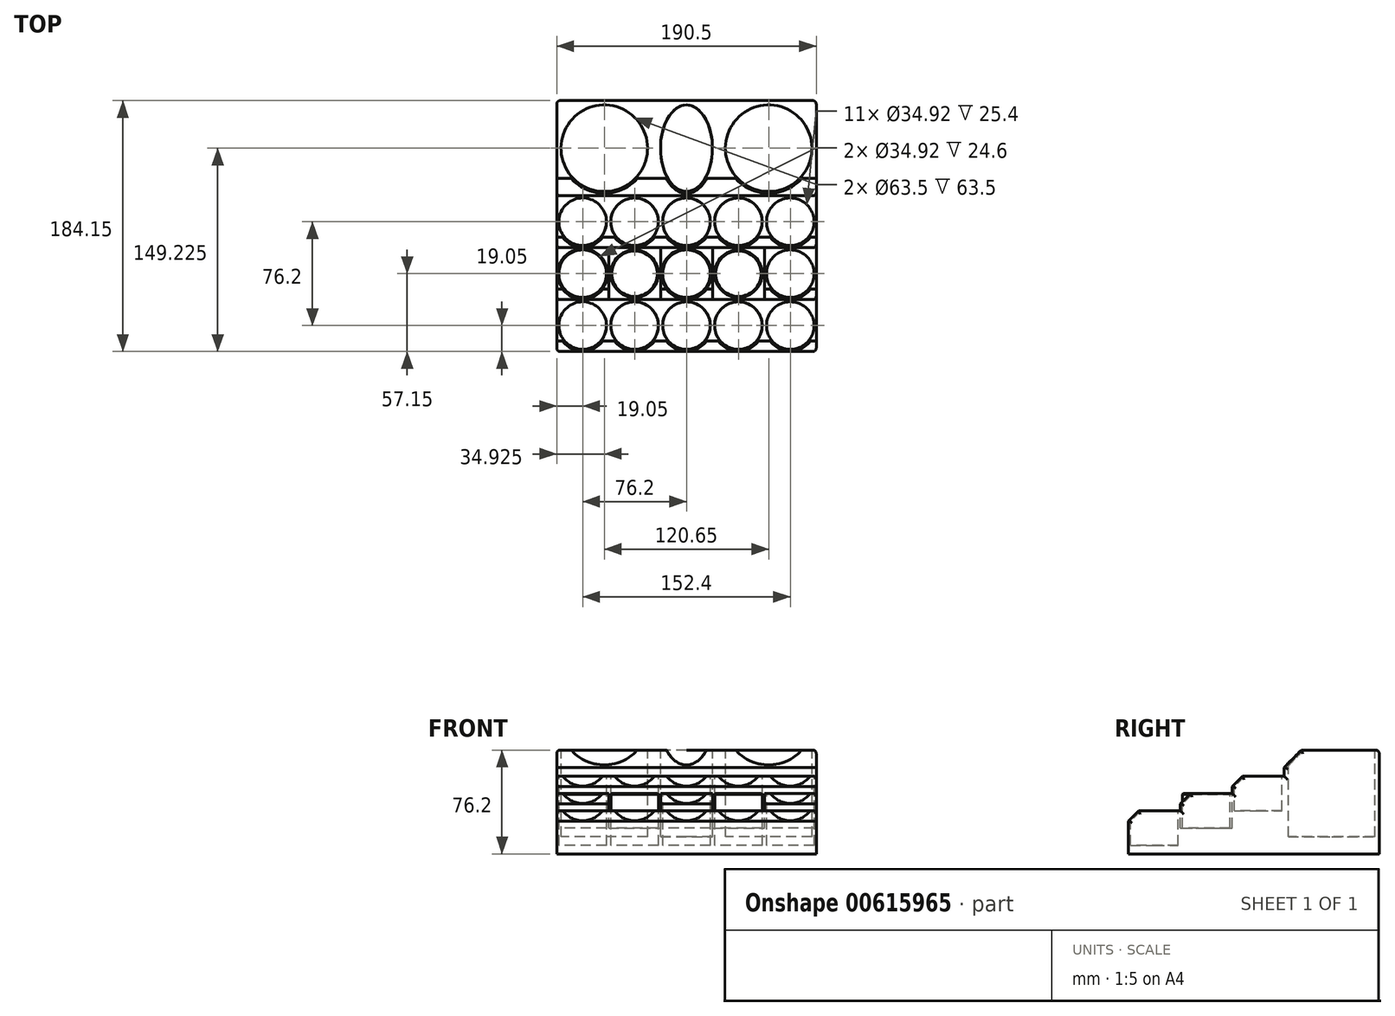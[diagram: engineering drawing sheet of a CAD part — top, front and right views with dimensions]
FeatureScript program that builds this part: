
annotation { "Feature Type Name" : "Feature", "Feature Type Description" : "" }
export const myFeature = defineFeature(function(context is Context, id is Id, definition is map)
    precondition{}
    {
        {
            var Q0;
            Q0=qCreatedBy(makeId("Right.planeOp"),FACE);
            var sketch = newSketch(context, id + "F0", { "sketchPlane" : qUnion([Q0])});
            skLineSegment(sketch, "E0", {"start": v(0, 0) * mm, "end": v(0, 31.75) * mm});
            skLineSegment(sketch, "E1", {"start": v(0, 31.75) * mm, "end": v(38.1, 31.75) * mm});
            skLineSegment(sketch, "E2", {"start": v(38.1, 31.75) * mm, "end": v(38.1, 44.45) * mm});
            skLineSegment(sketch, "E3", {"start": v(38.1, 44.45) * mm, "end": v(76.2, 44.45) * mm});
            skLineSegment(sketch, "E4", {"start": v(76.2, 44.45) * mm, "end": v(76.2, 57.15) * mm});
            skLineSegment(sketch, "E5", {"start": v(76.2, 57.15) * mm, "end": v(114.3, 57.15) * mm});
            skLineSegment(sketch, "E6", {"start": v(114.3, 57.15) * mm, "end": v(114.3, 76.2) * mm});
            skLineSegment(sketch, "E7", {"start": v(114.3, 76.2) * mm, "end": v(184.15, 76.2) * mm});
            skLineSegment(sketch, "E8", {"start": v(184.15, 76.2) * mm, "end": v(184.15, 0) * mm});
            skLineSegment(sketch, "E9", {"start": v(184.15, 0) * mm, "end": v(0, 0) * mm});
            skSolve(sketch);
        }
        {
            var Q0;
            Q0=qSketchRegion(id+"F0",true);
            extrude(context, id + "F1", {"entities" : qUnion([Q0]), "oppositeDirection" : true, "depth" : 190.5 * mm});
        }
        {
            var Q0;
            Q0=makeQuery(id+"F1.opExtrude","SWEPT_FACE",FACE,{"disambiguationData":[OSD([sQuery(id+"F0.wireOp",EDGE,"E1")])]});
            var sketch = newSketch(context, id + "F2", { "sketchPlane" : qUnion([Q0])});
            skLineSegment(sketch, "E10.bottom", {"start": v(-190.5, 0) * mm, "end": v(-152.4, 0) * mm, "construction": true});
            skLineSegment(sketch, "E10.top", {"start": v(-190.5, 38.1) * mm, "end": v(-152.4, 38.1) * mm, "construction": true});
            skLineSegment(sketch, "E10.left", {"start": v(-190.5, 0) * mm, "end": v(-190.5, 38.1) * mm, "construction": true});
            skLineSegment(sketch, "E10.right", {"start": v(-152.4, 0) * mm, "end": v(-152.4, 38.1) * mm, "construction": true});
            skLineSegment(sketch, "E11.bottom", {"start": v(-152.4, 0) * mm, "end": v(-114.3, 0) * mm, "construction": true});
            skLineSegment(sketch, "E11.top", {"start": v(-152.4, 38.1) * mm, "end": v(-114.3, 38.1) * mm, "construction": true});
            skLineSegment(sketch, "E11.right", {"start": v(-114.3, 0) * mm, "end": v(-114.3, 38.1) * mm, "construction": true});
            skLineSegment(sketch, "E12.bottom", {"start": v(-114.3, 0) * mm, "end": v(-76.2, 0) * mm, "construction": true});
            skLineSegment(sketch, "E12.top", {"start": v(-114.3, 38.1) * mm, "end": v(-76.2, 38.1) * mm, "construction": true});
            skLineSegment(sketch, "E12.right", {"start": v(-76.2, 0) * mm, "end": v(-76.2, 38.1) * mm, "construction": true});
            skLineSegment(sketch, "E13.bottom", {"start": v(-76.2, 0) * mm, "end": v(-38.1, 0) * mm, "construction": true});
            skLineSegment(sketch, "E13.top", {"start": v(-76.2, 38.1) * mm, "end": v(-38.1, 38.1) * mm, "construction": true});
            skLineSegment(sketch, "E13.right", {"start": v(-38.1, 0) * mm, "end": v(-38.1, 38.1) * mm, "construction": true});
            skLineSegment(sketch, "E14.bottom", {"start": v(-38.1, 0) * mm, "end": v(0, 0) * mm, "construction": true});
            skLineSegment(sketch, "E14.top", {"start": v(-38.1, 38.1) * mm, "end": v(0, 38.1) * mm, "construction": true});
            skLineSegment(sketch, "E14.right", {"start": v(0, 0) * mm, "end": v(0, 38.1) * mm, "construction": true});
            skLineSegment(sketch, "E15.bottom", {"start": v(-190.5, 0) * mm, "end": v(0, 0) * mm, "construction": true});
            skLineSegment(sketch, "E15.top", {"start": v(-190.5, 19.05) * mm, "end": v(0, 19.05) * mm, "construction": true});
            skLineSegment(sketch, "E15.left", {"start": v(-190.5, 0) * mm, "end": v(-190.5, 19.05) * mm, "construction": true});
            skLineSegment(sketch, "E15.right", {"start": v(0, 0) * mm, "end": v(0, 19.05) * mm, "construction": true});
            skLineSegment(sketch, "E16", {"start": v(-171.45, 0) * mm, "end": v(-171.45, 19.05) * mm, "construction": true});
            skLineSegment(sketch, "E17", {"start": v(-133.35, 0) * mm, "end": v(-133.35, 19.05) * mm, "construction": true});
            skLineSegment(sketch, "E18", {"start": v(-95.25, 0) * mm, "end": v(-95.25, 19.05) * mm, "construction": true});
            skLineSegment(sketch, "E19", {"start": v(-57.15, 0) * mm, "end": v(-57.15, 19.05) * mm, "construction": true});
            skLineSegment(sketch, "E20", {"start": v(-19.05, 0) * mm, "end": v(-19.05, 19.05) * mm, "construction": true});
            skCircle(sketch, "E21", {"center": v(-171.45, 19.05) * mm, "radius": 17.46 * mm});
            skCircle(sketch, "E22.MirrorC", {"center": v(-133.35, 19.05) * mm, "radius": 17.46 * mm});
            skCircle(sketch, "E23.MirrorC", {"center": v(-95.25, 19.05) * mm, "radius": 17.46 * mm});
            skCircle(sketch, "E24.MirrorC", {"center": v(-57.15, 19.05) * mm, "radius": 17.46 * mm});
            skCircle(sketch, "E25.MirrorC", {"center": v(-19.05, 19.05) * mm, "radius": 17.46 * mm});
            skSolve(sketch);
        }
        {
            var Q0;
            Q0=qSketchRegion(id+"F2",true);
            extrude(context, id + "F3", {"entities" : qUnion([Q0]), "operationType" : NewBodyOperationType.REMOVE, "oppositeDirection" : true, "depth" : 25.4 * mm});
        }
        {
            var Q0;
            Q0=makeQuery(id+"F1.opExtrude","SWEPT_FACE",FACE,{"disambiguationData":[OSD([sQuery(id+"F0.wireOp",EDGE,"E3")])]});
            var sketch = newSketch(context, id + "F4", { "sketchPlane" : qUnion([Q0])});
            skLineSegment(sketch, "E26.bottom", {"start": v(-190.5, 38.1) * mm, "end": v(-152.4, 38.1) * mm});
            skLineSegment(sketch, "E26.top", {"start": v(-190.5, 76.2) * mm, "end": v(-152.4, 76.2) * mm});
            skLineSegment(sketch, "E26.left", {"start": v(-190.5, 38.1) * mm, "end": v(-190.5, 76.2) * mm});
            skLineSegment(sketch, "E26.right", {"start": v(-152.4, 38.1) * mm, "end": v(-152.4, 76.2) * mm});
            skLineSegment(sketch, "E27.bottom", {"start": v(-152.4, 76.2) * mm, "end": v(-114.3, 76.2) * mm});
            skLineSegment(sketch, "E27.top", {"start": v(-152.4, 38.1) * mm, "end": v(-114.3, 38.1) * mm});
            skLineSegment(sketch, "E27.left", {"start": v(-152.4, 76.2) * mm, "end": v(-152.4, 38.1) * mm});
            skLineSegment(sketch, "E27.right", {"start": v(-114.3, 76.2) * mm, "end": v(-114.3, 38.1) * mm});
            skLineSegment(sketch, "E28.bottom", {"start": v(-114.3, 38.1) * mm, "end": v(-76.2, 38.1) * mm});
            skLineSegment(sketch, "E28.top", {"start": v(-114.3, 76.2) * mm, "end": v(-76.2, 76.2) * mm});
            skLineSegment(sketch, "E28.left", {"start": v(-114.3, 38.1) * mm, "end": v(-114.3, 76.2) * mm});
            skLineSegment(sketch, "E28.right", {"start": v(-76.2, 38.1) * mm, "end": v(-76.2, 76.2) * mm});
            skLineSegment(sketch, "E29.bottom", {"start": v(-76.2, 76.2) * mm, "end": v(-38.1, 76.2) * mm});
            skLineSegment(sketch, "E29.top", {"start": v(-76.2, 38.1) * mm, "end": v(-38.1, 38.1) * mm});
            skLineSegment(sketch, "E29.left", {"start": v(-76.2, 76.2) * mm, "end": v(-76.2, 38.1) * mm});
            skLineSegment(sketch, "E29.right", {"start": v(-38.1, 76.2) * mm, "end": v(-38.1, 38.1) * mm});
            skLineSegment(sketch, "E30.bottom", {"start": v(-38.1, 38.1) * mm, "end": v(0, 38.1) * mm});
            skLineSegment(sketch, "E30.top", {"start": v(-38.1, 76.2) * mm, "end": v(0, 76.2) * mm});
            skLineSegment(sketch, "E30.left", {"start": v(-38.1, 38.1) * mm, "end": v(-38.1, 76.2) * mm});
            skLineSegment(sketch, "E30.right", {"start": v(0, 38.1) * mm, "end": v(0, 76.2) * mm});
            skLineSegment(sketch, "E31", {"start": v(-190.5, 57.15) * mm, "end": v(0, 57.15) * mm, "construction": true});
            skLineSegment(sketch, "E32", {"start": v(-171.45, 76.2) * mm, "end": v(-171.45, 38.1) * mm, "construction": true});
            skLineSegment(sketch, "E33", {"start": v(-133.35, 76.2) * mm, "end": v(-133.35, 38.1) * mm, "construction": true});
            skLineSegment(sketch, "E34", {"start": v(-95.25, 76.2) * mm, "end": v(-95.25, 38.1) * mm, "construction": true});
            skLineSegment(sketch, "E35", {"start": v(-57.15, 76.2) * mm, "end": v(-57.15, 38.1) * mm, "construction": true});
            skLineSegment(sketch, "E36", {"start": v(-19.05, 76.2) * mm, "end": v(-19.05, 38.1) * mm, "construction": true});
            skCircle(sketch, "E37", {"center": v(-171.45, 57.15) * mm, "radius": 17.46 * mm});
            skCircle(sketch, "E38.MirrorC", {"center": v(-133.35, 57.15) * mm, "radius": 17.46 * mm});
            skCircle(sketch, "E39.MirrorC", {"center": v(-95.25, 57.15) * mm, "radius": 17.46 * mm});
            skCircle(sketch, "E40.MirrorC", {"center": v(-57.15, 57.15) * mm, "radius": 17.46 * mm});
            skCircle(sketch, "E41.MirrorC", {"center": v(-19.05, 57.15) * mm, "radius": 17.46 * mm});
            skSolve(sketch);
        }
        {
            var Q0;
            Q0=makeQuery(id+"F4.imprint","IMPRINT",FACE,{"disambiguationData":[TD([[makeQuery(id+"F4.imprint","IMPRINT",EDGE,{"derivedFrom":sQuery(id+"F4.wireOp",EDGE,"E39.MirrorC")}),1.0]])]});
            var Q1;
            Q1=makeQuery(id+"F4.imprint","IMPRINT",FACE,{"disambiguationData":[TD([[makeQuery(id+"F4.imprint","IMPRINT",EDGE,{"derivedFrom":sQuery(id+"F4.wireOp",EDGE,"E38.MirrorC")}),-1.0]])]});
            var Q2;
            Q2=makeQuery(id+"F4.imprint","IMPRINT",FACE,{"disambiguationData":[TD([[makeQuery(id+"F4.imprint","IMPRINT",EDGE,{"derivedFrom":sQuery(id+"F4.wireOp",EDGE,"E37")}),1.0]])]});
            var Q3;
            Q3=makeQuery(id+"F4.imprint","IMPRINT",FACE,{"disambiguationData":[TD([[makeQuery(id+"F4.imprint","IMPRINT",EDGE,{"derivedFrom":sQuery(id+"F4.wireOp",EDGE,"E40.MirrorC")}),-1.0]])]});
            var Q4;
            Q4=makeQuery(id+"F4.imprint","IMPRINT",FACE,{"disambiguationData":[TD([[makeQuery(id+"F4.imprint","IMPRINT",EDGE,{"derivedFrom":sQuery(id+"F4.wireOp",EDGE,"E41.MirrorC")}),1.0]])]});
            extrude(context, id + "F5", {"entities" : qUnion([Q0, Q1, Q2, Q3, Q4]), "operationType" : NewBodyOperationType.REMOVE, "oppositeDirection" : true, "depth" : 25.4 * mm});
        }
        {
            var Q0;
            Q0=makeQuery(id+"F1.opExtrude","SWEPT_FACE",FACE,{"disambiguationData":[OSD([sQuery(id+"F0.wireOp",EDGE,"E5")])]});
            var sketch = newSketch(context, id + "F6", { "sketchPlane" : qUnion([Q0])});
            skLineSegment(sketch, "E42.bottom", {"start": v(-190.5, 114.3) * mm, "end": v(-152.4, 114.3) * mm, "construction": true});
            skLineSegment(sketch, "E42.top", {"start": v(-190.5, 76.2) * mm, "end": v(-152.4, 76.2) * mm, "construction": true});
            skLineSegment(sketch, "E42.left", {"start": v(-190.5, 114.3) * mm, "end": v(-190.5, 76.2) * mm, "construction": true});
            skLineSegment(sketch, "E42.right", {"start": v(-152.4, 114.3) * mm, "end": v(-152.4, 76.2) * mm, "construction": true});
            skLineSegment(sketch, "E43.bottom", {"start": v(-152.4, 76.2) * mm, "end": v(-114.3, 76.2) * mm, "construction": true});
            skLineSegment(sketch, "E43.top", {"start": v(-152.4, 114.3) * mm, "end": v(-114.3, 114.3) * mm, "construction": true});
            skLineSegment(sketch, "E43.left", {"start": v(-152.4, 76.2) * mm, "end": v(-152.4, 114.3) * mm, "construction": true});
            skLineSegment(sketch, "E43.right", {"start": v(-114.3, 76.2) * mm, "end": v(-114.3, 114.3) * mm, "construction": true});
            skLineSegment(sketch, "E44.bottom", {"start": v(-114.3, 114.3) * mm, "end": v(-76.2, 114.3) * mm, "construction": true});
            skLineSegment(sketch, "E44.top", {"start": v(-114.3, 76.2) * mm, "end": v(-76.2, 76.2) * mm, "construction": true});
            skLineSegment(sketch, "E44.left", {"start": v(-114.3, 114.3) * mm, "end": v(-114.3, 76.2) * mm, "construction": true});
            skLineSegment(sketch, "E44.right", {"start": v(-76.2, 114.3) * mm, "end": v(-76.2, 76.2) * mm, "construction": true});
            skLineSegment(sketch, "E45.bottom", {"start": v(-76.2, 76.2) * mm, "end": v(-38.1, 76.2) * mm, "construction": true});
            skLineSegment(sketch, "E45.top", {"start": v(-76.2, 114.3) * mm, "end": v(-38.1, 114.3) * mm, "construction": true});
            skLineSegment(sketch, "E45.left", {"start": v(-76.2, 76.2) * mm, "end": v(-76.2, 114.3) * mm, "construction": true});
            skLineSegment(sketch, "E45.right", {"start": v(-38.1, 76.2) * mm, "end": v(-38.1, 114.3) * mm, "construction": true});
            skLineSegment(sketch, "E46.bottom", {"start": v(-38.1, 114.3) * mm, "end": v(0, 114.3) * mm, "construction": true});
            skLineSegment(sketch, "E46.top", {"start": v(-38.1, 76.2) * mm, "end": v(0, 76.2) * mm, "construction": true});
            skLineSegment(sketch, "E46.left", {"start": v(-38.1, 114.3) * mm, "end": v(-38.1, 76.2) * mm, "construction": true});
            skLineSegment(sketch, "E46.right", {"start": v(0, 114.3) * mm, "end": v(0, 76.2) * mm, "construction": true});
            skLineSegment(sketch, "E47", {"start": v(-190.5, 95.25) * mm, "end": v(0, 95.25) * mm, "construction": true});
            skLineSegment(sketch, "E48", {"start": v(-171.45, 76.2) * mm, "end": v(-171.45, 114.3) * mm, "construction": true});
            skLineSegment(sketch, "E49", {"start": v(-133.35, 114.3) * mm, "end": v(-133.35, 76.2) * mm, "construction": true});
            skLineSegment(sketch, "E50", {"start": v(-95.25, 114.3) * mm, "end": v(-95.25, 76.2) * mm, "construction": true});
            skLineSegment(sketch, "E51", {"start": v(-57.15, 114.3) * mm, "end": v(-57.15, 76.2) * mm, "construction": true});
            skLineSegment(sketch, "E52", {"start": v(-19.05, 114.3) * mm, "end": v(-19.05, 76.2) * mm, "construction": true});
            skCircle(sketch, "E53", {"center": v(-171.45, 95.25) * mm, "radius": 17.46 * mm});
            skCircle(sketch, "E54.MirrorC", {"center": v(-133.35, 95.25) * mm, "radius": 17.46 * mm});
            skCircle(sketch, "E55.MirrorC", {"center": v(-95.25, 95.25) * mm, "radius": 17.46 * mm});
            skCircle(sketch, "E56.MirrorC", {"center": v(-57.15, 95.25) * mm, "radius": 17.46 * mm});
            skCircle(sketch, "E57.MirrorC", {"center": v(-19.05, 95.25) * mm, "radius": 17.46 * mm});
            skSolve(sketch);
        }
        {
            var Q0;
            Q0=qSketchRegion(id+"F6",true);
            extrude(context, id + "F7", {"entities" : qUnion([Q0]), "operationType" : NewBodyOperationType.REMOVE, "oppositeDirection" : true, "depth" : 25.4 * mm});
        }
        {
            var Q0;
            Q0=makeQuery(id+"F1.opExtrude","SWEPT_FACE",FACE,{"disambiguationData":[OSD([sQuery(id+"F0.wireOp",EDGE,"E7")])]});
            var sketch = newSketch(context, id + "F8", { "sketchPlane" : qUnion([Q0])});
            skLineSegment(sketch, "E58.bottom", {"start": v(-190.5, 114.3) * mm, "end": v(-120.65, 114.3) * mm, "construction": true});
            skLineSegment(sketch, "E58.top", {"start": v(-190.5, 184.15) * mm, "end": v(-120.65, 184.15) * mm, "construction": true});
            skLineSegment(sketch, "E58.left", {"start": v(-190.5, 114.3) * mm, "end": v(-190.5, 184.15) * mm, "construction": true});
            skLineSegment(sketch, "E58.right", {"start": v(-120.65, 114.3) * mm, "end": v(-120.65, 184.15) * mm, "construction": true});
            skLineSegment(sketch, "E59.bottom", {"start": v(0, 114.3) * mm, "end": v(-69.85, 114.3) * mm, "construction": true});
            skLineSegment(sketch, "E59.top", {"start": v(0, 184.15) * mm, "end": v(-69.85, 184.15) * mm, "construction": true});
            skLineSegment(sketch, "E59.left", {"start": v(0, 114.3) * mm, "end": v(0, 184.15) * mm, "construction": true});
            skLineSegment(sketch, "E59.right", {"start": v(-69.85, 114.3) * mm, "end": v(-69.85, 184.15) * mm, "construction": true});
            skLineSegment(sketch, "E60", {"start": v(-155.58, 114.3) * mm, "end": v(-155.58, 184.15) * mm, "construction": true});
            skLineSegment(sketch, "E61", {"start": v(-34.93, 184.15) * mm, "end": v(-34.93, 114.3) * mm, "construction": true});
            skLineSegment(sketch, "E62", {"start": v(-190.5, 149.23) * mm, "end": v(0, 149.23) * mm, "construction": true});
            skLineSegment(sketch, "E63", {"start": v(-95.25, 184.15) * mm, "end": v(-95.25, 114.3) * mm, "construction": true});
            skCircle(sketch, "E64", {"center": v(-155.58, 149.23) * mm, "radius": 31.75 * mm});
            skCircle(sketch, "E65.MirrorC", {"center": v(-34.93, 149.23) * mm, "radius": 31.75 * mm});
            skEllipse(sketch, "E66", {"center": v(-95.25, 149.23) * mm, "majorRadius": 31.75 * mm, "minorRadius": 19.05 * mm, "majorAxis": v(0, 1)});
            skSolve(sketch);
        }
        {
            var Q0;
            Q0=qSketchRegion(id+"F8",true);
            extrude(context, id + "F9", {"entities" : qUnion([Q0]), "operationType" : NewBodyOperationType.REMOVE, "oppositeDirection" : true, "depth" : 63.5 * mm});
        }
        {
            var Q0;
            Q0=makeQuery(id+"F1.opExtrude","SWEPT_EDGE",EDGE,{"disambiguationData":[OSD([sQuery(id+"F0.wireOp",EDGE,"E4"),sQuery(id+"F0.wireOp",EDGE,"E5")])]});
            var Q1;
            Q1=makeQuery(id+"F1.opExtrude","SWEPT_EDGE",EDGE,{"disambiguationData":[OSD([sQuery(id+"F0.wireOp",EDGE,"E2"),sQuery(id+"F0.wireOp",EDGE,"E3")])]});
            var Q2;
            Q2=makeQuery(id+"F1.opExtrude","SWEPT_EDGE",EDGE,{"disambiguationData":[OSD([sQuery(id+"F0.wireOp",EDGE,"E0"),sQuery(id+"F0.wireOp",EDGE,"E1")])]});
            chamfer(context, id + "F10", {"entities" : qUnion([Q0, Q1, Q2]), "width" : 7.62 * mm});
        }
        {
            var Q0;
            Q0=makeQuery(id+"F1.opExtrude","SWEPT_EDGE",EDGE,{"disambiguationData":[OSD([sQuery(id+"F0.wireOp",EDGE,"E6"),sQuery(id+"F0.wireOp",EDGE,"E7")])]});
            chamfer(context, id + "F11", {"entities" : qUnion([Q0]), "width" : 12.7 * mm, "tangentPropagation" : true});
        }
        {
            var Q0;
            Q0=makeQuery(id+"F3.boolean.opBoolean","COPY",EDGE,{"derivedFrom":makeQuery(id+"F3.opExtrude","CAP_EDGE",EDGE,{"disambiguationData":[OSD([sQuery(id+"F2.wireOp",EDGE,"E21")])],"isStart":true})});
            var Q1;
            Q1=makeQuery(id+"F3.boolean.opBoolean","COPY",EDGE,{"derivedFrom":makeQuery(id+"F3.opExtrude","CAP_EDGE",EDGE,{"disambiguationData":[OSD([sQuery(id+"F2.wireOp",EDGE,"E22.MirrorC")])],"isStart":true})});
            var Q2;
            Q2=makeQuery(id+"F3.boolean.opBoolean","COPY",EDGE,{"derivedFrom":makeQuery(id+"F3.opExtrude","CAP_EDGE",EDGE,{"disambiguationData":[OSD([sQuery(id+"F2.wireOp",EDGE,"E23.MirrorC")])],"isStart":true})});
            var Q3;
            Q3=makeQuery(id+"F3.boolean.opBoolean","COPY",EDGE,{"derivedFrom":makeQuery(id+"F3.opExtrude","CAP_EDGE",EDGE,{"disambiguationData":[OSD([sQuery(id+"F2.wireOp",EDGE,"E24.MirrorC")])],"isStart":true})});
            var Q4;
            Q4=makeQuery(id+"F3.boolean.opBoolean","COPY",EDGE,{"derivedFrom":makeQuery(id+"F3.opExtrude","CAP_EDGE",EDGE,{"disambiguationData":[OSD([sQuery(id+"F2.wireOp",EDGE,"E25.MirrorC")])],"isStart":true})});
            var Q5;
            Q5=makeQuery(id+"F5.boolean.opBoolean","COPY",EDGE,{"derivedFrom":makeQuery(id+"F5.opExtrude","CAP_EDGE",EDGE,{"disambiguationData":[OSD([sQuery(id+"F4.wireOp",EDGE,"E41.MirrorC")])],"isStart":true})});
            var Q6;
            Q6=makeQuery(id+"F5.boolean.opBoolean","COPY",EDGE,{"derivedFrom":makeQuery(id+"F5.opExtrude","CAP_EDGE",EDGE,{"disambiguationData":[OSD([sQuery(id+"F4.wireOp",EDGE,"E40.MirrorC")])],"isStart":true})});
            var Q7;
            Q7=makeQuery(id+"F5.boolean.opBoolean","COPY",EDGE,{"derivedFrom":makeQuery(id+"F5.opExtrude","CAP_EDGE",EDGE,{"disambiguationData":[OSD([sQuery(id+"F4.wireOp",EDGE,"E39.MirrorC")])],"isStart":true})});
            var Q8;
            Q8=makeQuery(id+"F5.boolean.opBoolean","COPY",EDGE,{"derivedFrom":makeQuery(id+"F5.opExtrude","CAP_EDGE",EDGE,{"disambiguationData":[OSD([sQuery(id+"F4.wireOp",EDGE,"E38.MirrorC")])],"isStart":true})});
            var Q9;
            Q9=makeQuery(id+"F5.boolean.opBoolean","COPY",EDGE,{"derivedFrom":makeQuery(id+"F5.opExtrude","CAP_EDGE",EDGE,{"disambiguationData":[OSD([sQuery(id+"F4.wireOp",EDGE,"E37")])],"isStart":true})});
            var Q10;
            Q10=makeQuery(id+"F7.boolean.opBoolean","COPY",EDGE,{"derivedFrom":makeQuery(id+"F7.opExtrude","CAP_EDGE",EDGE,{"disambiguationData":[OSD([sQuery(id+"F6.wireOp",EDGE,"E53")])],"isStart":true})});
            var Q11;
            Q11=makeQuery(id+"F7.boolean.opBoolean","COPY",EDGE,{"derivedFrom":makeQuery(id+"F7.opExtrude","CAP_EDGE",EDGE,{"disambiguationData":[OSD([sQuery(id+"F6.wireOp",EDGE,"E54.MirrorC")])],"isStart":true})});
            var Q12;
            Q12=makeQuery(id+"F7.boolean.opBoolean","COPY",EDGE,{"derivedFrom":makeQuery(id+"F7.opExtrude","CAP_EDGE",EDGE,{"disambiguationData":[OSD([sQuery(id+"F6.wireOp",EDGE,"E55.MirrorC")])],"isStart":true})});
            var Q13;
            Q13=makeQuery(id+"F7.boolean.opBoolean","COPY",EDGE,{"derivedFrom":makeQuery(id+"F7.opExtrude","CAP_EDGE",EDGE,{"disambiguationData":[OSD([sQuery(id+"F6.wireOp",EDGE,"E56.MirrorC")])],"isStart":true})});
            var Q14;
            Q14=makeQuery(id+"F7.boolean.opBoolean","COPY",EDGE,{"derivedFrom":makeQuery(id+"F7.opExtrude","CAP_EDGE",EDGE,{"disambiguationData":[OSD([sQuery(id+"F6.wireOp",EDGE,"E57.MirrorC")])],"isStart":true})});
            var Q15;
            Q15=makeQuery(id+"F9.boolean.opBoolean","COPY",EDGE,{"derivedFrom":makeQuery(id+"F9.opExtrude","CAP_EDGE",EDGE,{"disambiguationData":[OSD([sQuery(id+"F8.wireOp",EDGE,"E65.MirrorC")])],"isStart":true})});
            var Q16;
            Q16=makeQuery(id+"F9.boolean.opBoolean","COPY",EDGE,{"derivedFrom":makeQuery(id+"F9.opExtrude","CAP_EDGE",EDGE,{"disambiguationData":[OSD([sQuery(id+"F8.wireOp",EDGE,"E66")])],"isStart":true})});
            var Q17;
            Q17=makeQuery(id+"F9.boolean.opBoolean","COPY",EDGE,{"derivedFrom":makeQuery(id+"F9.opExtrude","CAP_EDGE",EDGE,{"disambiguationData":[OSD([sQuery(id+"F8.wireOp",EDGE,"E64")])],"isStart":true})});
            var Q18;
            Q18=makeQuery(id+"F10.opChamfer","BLEND_EDGE",EDGE,{"blendedFrom":[makeQuery(id+"F1.opExtrude","SWEPT_EDGE",EDGE,{"disambiguationData":[OSD([sQuery(id+"F0.wireOp",EDGE,"E0"),sQuery(id+"F0.wireOp",EDGE,"E1")])]}),makeQuery(id+"F3.boolean.opBoolean","COPY",FACE,{"derivedFrom":makeQuery(id+"F3.opExtrude","SWEPT_FACE",FACE,{"disambiguationData":[OSD([sQuery(id+"F2.wireOp",EDGE,"E21")])]})})],"blendedInto":[makeQuery(id+"F3.boolean.opBoolean","COPY",FACE,{"derivedFrom":makeQuery(id+"F3.opExtrude","SWEPT_FACE",FACE,{"disambiguationData":[OSD([sQuery(id+"F2.wireOp",EDGE,"E21")])]})})]});
            var Q19;
            Q19=makeQuery(id+"F10.opChamfer","BLEND_EDGE",EDGE,{"blendedFrom":[makeQuery(id+"F1.opExtrude","SWEPT_EDGE",EDGE,{"disambiguationData":[OSD([sQuery(id+"F0.wireOp",EDGE,"E0"),sQuery(id+"F0.wireOp",EDGE,"E1")])]}),makeQuery(id+"F3.boolean.opBoolean","COPY",FACE,{"derivedFrom":makeQuery(id+"F3.opExtrude","SWEPT_FACE",FACE,{"disambiguationData":[OSD([sQuery(id+"F2.wireOp",EDGE,"E22.MirrorC")])]})})],"blendedInto":[makeQuery(id+"F3.boolean.opBoolean","COPY",FACE,{"derivedFrom":makeQuery(id+"F3.opExtrude","SWEPT_FACE",FACE,{"disambiguationData":[OSD([sQuery(id+"F2.wireOp",EDGE,"E22.MirrorC")])]})})]});
            var Q20;
            Q20=makeQuery(id+"F10.opChamfer","BLEND_EDGE",EDGE,{"blendedFrom":[makeQuery(id+"F1.opExtrude","SWEPT_EDGE",EDGE,{"disambiguationData":[OSD([sQuery(id+"F0.wireOp",EDGE,"E0"),sQuery(id+"F0.wireOp",EDGE,"E1")])]}),makeQuery(id+"F3.boolean.opBoolean","COPY",FACE,{"derivedFrom":makeQuery(id+"F3.opExtrude","SWEPT_FACE",FACE,{"disambiguationData":[OSD([sQuery(id+"F2.wireOp",EDGE,"E23.MirrorC")])]})})],"blendedInto":[makeQuery(id+"F3.boolean.opBoolean","COPY",FACE,{"derivedFrom":makeQuery(id+"F3.opExtrude","SWEPT_FACE",FACE,{"disambiguationData":[OSD([sQuery(id+"F2.wireOp",EDGE,"E23.MirrorC")])]})})]});
            var Q21;
            Q21=makeQuery(id+"F10.opChamfer","BLEND_EDGE",EDGE,{"blendedFrom":[makeQuery(id+"F1.opExtrude","SWEPT_EDGE",EDGE,{"disambiguationData":[OSD([sQuery(id+"F0.wireOp",EDGE,"E0"),sQuery(id+"F0.wireOp",EDGE,"E1")])]}),makeQuery(id+"F3.boolean.opBoolean","COPY",FACE,{"derivedFrom":makeQuery(id+"F3.opExtrude","SWEPT_FACE",FACE,{"disambiguationData":[OSD([sQuery(id+"F2.wireOp",EDGE,"E24.MirrorC")])]})})],"blendedInto":[makeQuery(id+"F3.boolean.opBoolean","COPY",FACE,{"derivedFrom":makeQuery(id+"F3.opExtrude","SWEPT_FACE",FACE,{"disambiguationData":[OSD([sQuery(id+"F2.wireOp",EDGE,"E24.MirrorC")])]})})]});
            var Q22;
            Q22=makeQuery(id+"F10.opChamfer","BLEND_EDGE",EDGE,{"blendedFrom":[makeQuery(id+"F1.opExtrude","SWEPT_EDGE",EDGE,{"disambiguationData":[OSD([sQuery(id+"F0.wireOp",EDGE,"E0"),sQuery(id+"F0.wireOp",EDGE,"E1")])]}),makeQuery(id+"F3.boolean.opBoolean","COPY",FACE,{"derivedFrom":makeQuery(id+"F3.opExtrude","SWEPT_FACE",FACE,{"disambiguationData":[OSD([sQuery(id+"F2.wireOp",EDGE,"E25.MirrorC")])]})})],"blendedInto":[makeQuery(id+"F3.boolean.opBoolean","COPY",FACE,{"derivedFrom":makeQuery(id+"F3.opExtrude","SWEPT_FACE",FACE,{"disambiguationData":[OSD([sQuery(id+"F2.wireOp",EDGE,"E25.MirrorC")])]})})]});
            var Q23;
            Q23=makeQuery(id+"F10.opChamfer","BLEND_EDGE",EDGE,{"blendedFrom":[makeQuery(id+"F1.opExtrude","SWEPT_EDGE",EDGE,{"disambiguationData":[OSD([sQuery(id+"F0.wireOp",EDGE,"E2"),sQuery(id+"F0.wireOp",EDGE,"E3")])]}),makeQuery(id+"F5.boolean.opBoolean","COPY",FACE,{"derivedFrom":makeQuery(id+"F5.opExtrude","SWEPT_FACE",FACE,{"disambiguationData":[OSD([sQuery(id+"F4.wireOp",EDGE,"E41.MirrorC")])]})})],"blendedInto":[makeQuery(id+"F5.boolean.opBoolean","COPY",FACE,{"derivedFrom":makeQuery(id+"F5.opExtrude","SWEPT_FACE",FACE,{"disambiguationData":[OSD([sQuery(id+"F4.wireOp",EDGE,"E41.MirrorC")])]})})]});
            var Q24;
            Q24=makeQuery(id+"F10.opChamfer","BLEND_EDGE",EDGE,{"blendedFrom":[makeQuery(id+"F1.opExtrude","SWEPT_EDGE",EDGE,{"disambiguationData":[OSD([sQuery(id+"F0.wireOp",EDGE,"E2"),sQuery(id+"F0.wireOp",EDGE,"E3")])]}),makeQuery(id+"F5.boolean.opBoolean","COPY",FACE,{"derivedFrom":makeQuery(id+"F5.opExtrude","SWEPT_FACE",FACE,{"disambiguationData":[OSD([sQuery(id+"F4.wireOp",EDGE,"E40.MirrorC")])]})})],"blendedInto":[makeQuery(id+"F5.boolean.opBoolean","COPY",FACE,{"derivedFrom":makeQuery(id+"F5.opExtrude","SWEPT_FACE",FACE,{"disambiguationData":[OSD([sQuery(id+"F4.wireOp",EDGE,"E40.MirrorC")])]})})]});
            var Q25;
            Q25=makeQuery(id+"F10.opChamfer","BLEND_EDGE",EDGE,{"blendedFrom":[makeQuery(id+"F1.opExtrude","SWEPT_EDGE",EDGE,{"disambiguationData":[OSD([sQuery(id+"F0.wireOp",EDGE,"E2"),sQuery(id+"F0.wireOp",EDGE,"E3")])]}),makeQuery(id+"F5.boolean.opBoolean","COPY",FACE,{"derivedFrom":makeQuery(id+"F5.opExtrude","SWEPT_FACE",FACE,{"disambiguationData":[OSD([sQuery(id+"F4.wireOp",EDGE,"E39.MirrorC")])]})})],"blendedInto":[makeQuery(id+"F5.boolean.opBoolean","COPY",FACE,{"derivedFrom":makeQuery(id+"F5.opExtrude","SWEPT_FACE",FACE,{"disambiguationData":[OSD([sQuery(id+"F4.wireOp",EDGE,"E39.MirrorC")])]})})]});
            var Q26;
            Q26=makeQuery(id+"F10.opChamfer","BLEND_EDGE",EDGE,{"blendedFrom":[makeQuery(id+"F1.opExtrude","SWEPT_EDGE",EDGE,{"disambiguationData":[OSD([sQuery(id+"F0.wireOp",EDGE,"E2"),sQuery(id+"F0.wireOp",EDGE,"E3")])]}),makeQuery(id+"F5.boolean.opBoolean","COPY",FACE,{"derivedFrom":makeQuery(id+"F5.opExtrude","SWEPT_FACE",FACE,{"disambiguationData":[OSD([sQuery(id+"F4.wireOp",EDGE,"E38.MirrorC")])]})})],"blendedInto":[makeQuery(id+"F5.boolean.opBoolean","COPY",FACE,{"derivedFrom":makeQuery(id+"F5.opExtrude","SWEPT_FACE",FACE,{"disambiguationData":[OSD([sQuery(id+"F4.wireOp",EDGE,"E38.MirrorC")])]})})]});
            var Q27;
            Q27=makeQuery(id+"F10.opChamfer","BLEND_EDGE",EDGE,{"blendedFrom":[makeQuery(id+"F1.opExtrude","SWEPT_EDGE",EDGE,{"disambiguationData":[OSD([sQuery(id+"F0.wireOp",EDGE,"E2"),sQuery(id+"F0.wireOp",EDGE,"E3")])]}),makeQuery(id+"F5.boolean.opBoolean","COPY",FACE,{"derivedFrom":makeQuery(id+"F5.opExtrude","SWEPT_FACE",FACE,{"disambiguationData":[OSD([sQuery(id+"F4.wireOp",EDGE,"E37")])]})})],"blendedInto":[makeQuery(id+"F5.boolean.opBoolean","COPY",FACE,{"derivedFrom":makeQuery(id+"F5.opExtrude","SWEPT_FACE",FACE,{"disambiguationData":[OSD([sQuery(id+"F4.wireOp",EDGE,"E37")])]})})]});
            var Q28;
            Q28=makeQuery(id+"F10.opChamfer","BLEND_EDGE",EDGE,{"blendedFrom":[makeQuery(id+"F1.opExtrude","SWEPT_EDGE",EDGE,{"disambiguationData":[OSD([sQuery(id+"F0.wireOp",EDGE,"E4"),sQuery(id+"F0.wireOp",EDGE,"E5")])]}),makeQuery(id+"F7.boolean.opBoolean","COPY",FACE,{"derivedFrom":makeQuery(id+"F7.opExtrude","SWEPT_FACE",FACE,{"disambiguationData":[OSD([sQuery(id+"F6.wireOp",EDGE,"E53")])]})})],"blendedInto":[makeQuery(id+"F7.boolean.opBoolean","COPY",FACE,{"derivedFrom":makeQuery(id+"F7.opExtrude","SWEPT_FACE",FACE,{"disambiguationData":[OSD([sQuery(id+"F6.wireOp",EDGE,"E53")])]})})]});
            var Q29;
            Q29=makeQuery(id+"F10.opChamfer","BLEND_EDGE",EDGE,{"blendedFrom":[makeQuery(id+"F1.opExtrude","SWEPT_EDGE",EDGE,{"disambiguationData":[OSD([sQuery(id+"F0.wireOp",EDGE,"E4"),sQuery(id+"F0.wireOp",EDGE,"E5")])]}),makeQuery(id+"F7.boolean.opBoolean","COPY",FACE,{"derivedFrom":makeQuery(id+"F7.opExtrude","SWEPT_FACE",FACE,{"disambiguationData":[OSD([sQuery(id+"F6.wireOp",EDGE,"E54.MirrorC")])]})})],"blendedInto":[makeQuery(id+"F7.boolean.opBoolean","COPY",FACE,{"derivedFrom":makeQuery(id+"F7.opExtrude","SWEPT_FACE",FACE,{"disambiguationData":[OSD([sQuery(id+"F6.wireOp",EDGE,"E54.MirrorC")])]})})]});
            var Q30;
            Q30=makeQuery(id+"F10.opChamfer","BLEND_EDGE",EDGE,{"blendedFrom":[makeQuery(id+"F1.opExtrude","SWEPT_EDGE",EDGE,{"disambiguationData":[OSD([sQuery(id+"F0.wireOp",EDGE,"E4"),sQuery(id+"F0.wireOp",EDGE,"E5")])]}),makeQuery(id+"F7.boolean.opBoolean","COPY",FACE,{"derivedFrom":makeQuery(id+"F7.opExtrude","SWEPT_FACE",FACE,{"disambiguationData":[OSD([sQuery(id+"F6.wireOp",EDGE,"E55.MirrorC")])]})})],"blendedInto":[makeQuery(id+"F7.boolean.opBoolean","COPY",FACE,{"derivedFrom":makeQuery(id+"F7.opExtrude","SWEPT_FACE",FACE,{"disambiguationData":[OSD([sQuery(id+"F6.wireOp",EDGE,"E55.MirrorC")])]})})]});
            var Q31;
            Q31=makeQuery(id+"F10.opChamfer","BLEND_EDGE",EDGE,{"blendedFrom":[makeQuery(id+"F1.opExtrude","SWEPT_EDGE",EDGE,{"disambiguationData":[OSD([sQuery(id+"F0.wireOp",EDGE,"E4"),sQuery(id+"F0.wireOp",EDGE,"E5")])]}),makeQuery(id+"F7.boolean.opBoolean","COPY",FACE,{"derivedFrom":makeQuery(id+"F7.opExtrude","SWEPT_FACE",FACE,{"disambiguationData":[OSD([sQuery(id+"F6.wireOp",EDGE,"E56.MirrorC")])]})})],"blendedInto":[makeQuery(id+"F7.boolean.opBoolean","COPY",FACE,{"derivedFrom":makeQuery(id+"F7.opExtrude","SWEPT_FACE",FACE,{"disambiguationData":[OSD([sQuery(id+"F6.wireOp",EDGE,"E56.MirrorC")])]})})]});
            var Q32;
            Q32=makeQuery(id+"F10.opChamfer","BLEND_EDGE",EDGE,{"blendedFrom":[makeQuery(id+"F1.opExtrude","SWEPT_EDGE",EDGE,{"disambiguationData":[OSD([sQuery(id+"F0.wireOp",EDGE,"E4"),sQuery(id+"F0.wireOp",EDGE,"E5")])]}),makeQuery(id+"F7.boolean.opBoolean","COPY",FACE,{"derivedFrom":makeQuery(id+"F7.opExtrude","SWEPT_FACE",FACE,{"disambiguationData":[OSD([sQuery(id+"F6.wireOp",EDGE,"E57.MirrorC")])]})})],"blendedInto":[makeQuery(id+"F7.boolean.opBoolean","COPY",FACE,{"derivedFrom":makeQuery(id+"F7.opExtrude","SWEPT_FACE",FACE,{"disambiguationData":[OSD([sQuery(id+"F6.wireOp",EDGE,"E57.MirrorC")])]})})]});
            var Q33;
            Q33=makeQuery(id+"F11.opChamfer","BLEND_EDGE",EDGE,{"blendedFrom":[makeQuery(id+"F1.opExtrude","SWEPT_EDGE",EDGE,{"disambiguationData":[OSD([sQuery(id+"F0.wireOp",EDGE,"E6"),sQuery(id+"F0.wireOp",EDGE,"E7")])]}),makeQuery(id+"F9.boolean.opBoolean","COPY",FACE,{"derivedFrom":makeQuery(id+"F9.opExtrude","SWEPT_FACE",FACE,{"disambiguationData":[OSD([sQuery(id+"F8.wireOp",EDGE,"E65.MirrorC")])]})})],"blendedInto":[makeQuery(id+"F9.boolean.opBoolean","COPY",FACE,{"derivedFrom":makeQuery(id+"F9.opExtrude","SWEPT_FACE",FACE,{"disambiguationData":[OSD([sQuery(id+"F8.wireOp",EDGE,"E65.MirrorC")])]})})]});
            var Q34;
            Q34=makeQuery(id+"F11.opChamfer","BLEND_EDGE",EDGE,{"blendedFrom":[makeQuery(id+"F1.opExtrude","SWEPT_EDGE",EDGE,{"disambiguationData":[OSD([sQuery(id+"F0.wireOp",EDGE,"E6"),sQuery(id+"F0.wireOp",EDGE,"E7")])]}),makeQuery(id+"F9.boolean.opBoolean","COPY",FACE,{"derivedFrom":makeQuery(id+"F9.opExtrude","SWEPT_FACE",FACE,{"disambiguationData":[OSD([sQuery(id+"F8.wireOp",EDGE,"E66")])]})})],"blendedInto":[makeQuery(id+"F9.boolean.opBoolean","COPY",FACE,{"derivedFrom":makeQuery(id+"F9.opExtrude","SWEPT_FACE",FACE,{"disambiguationData":[OSD([sQuery(id+"F8.wireOp",EDGE,"E66")])]})})]});
            var Q35;
            Q35=makeQuery(id+"F11.opChamfer","BLEND_EDGE",EDGE,{"blendedFrom":[makeQuery(id+"F1.opExtrude","SWEPT_EDGE",EDGE,{"disambiguationData":[OSD([sQuery(id+"F0.wireOp",EDGE,"E6"),sQuery(id+"F0.wireOp",EDGE,"E7")])]}),makeQuery(id+"F9.boolean.opBoolean","COPY",FACE,{"derivedFrom":makeQuery(id+"F9.opExtrude","SWEPT_FACE",FACE,{"disambiguationData":[OSD([sQuery(id+"F8.wireOp",EDGE,"E64")])]})})],"blendedInto":[makeQuery(id+"F9.boolean.opBoolean","COPY",FACE,{"derivedFrom":makeQuery(id+"F9.opExtrude","SWEPT_FACE",FACE,{"disambiguationData":[OSD([sQuery(id+"F8.wireOp",EDGE,"E64")])]})})]});
            chamfer(context, id + "F12", {"entities" : qUnion([Q0, Q1, Q2, Q3, Q4, Q5, Q6, Q7, Q8, Q9, Q10, Q11, Q12, Q13, Q14, Q15, Q16, Q17, Q18, Q19, Q20, Q21, Q22, Q23, Q24, Q25, Q26, Q27, Q28, Q29, Q30, Q31, Q32, Q33, Q34, Q35]), "width" : 0.8 * mm, "tangentPropagation" : true});
        }
        {
            var Q0;
            Q0=makeQuery(id+"F1.opExtrude","CAP_EDGE",EDGE,{"disambiguationData":[OSD([sQuery(id+"F0.wireOp",EDGE,"E0")])],"isStart":true});
            var Q1;
            Q1=makeQuery(id+"F1.opExtrude","CAP_EDGE",EDGE,{"disambiguationData":[OSD([sQuery(id+"F0.wireOp",EDGE,"E1")])],"isStart":true});
            var Q2;
            Q2=makeQuery(id+"F1.opExtrude","CAP_EDGE",EDGE,{"disambiguationData":[OSD([sQuery(id+"F0.wireOp",EDGE,"E2")])],"isStart":true});
            var Q3;
            Q3=makeQuery(id+"F1.opExtrude","CAP_EDGE",EDGE,{"disambiguationData":[OSD([sQuery(id+"F0.wireOp",EDGE,"E3")])],"isStart":true});
            var Q4;
            Q4=makeQuery(id+"F1.opExtrude","CAP_EDGE",EDGE,{"disambiguationData":[OSD([sQuery(id+"F0.wireOp",EDGE,"E4")])],"isStart":true});
            var Q5;
            Q5=makeQuery(id+"F1.opExtrude","CAP_EDGE",EDGE,{"disambiguationData":[OSD([sQuery(id+"F0.wireOp",EDGE,"E5")])],"isStart":true});
            var Q6;
            Q6=makeQuery(id+"F1.opExtrude","CAP_EDGE",EDGE,{"disambiguationData":[OSD([sQuery(id+"F0.wireOp",EDGE,"E6")])],"isStart":true});
            var Q7;
            Q7=makeQuery(id+"F1.opExtrude","CAP_EDGE",EDGE,{"disambiguationData":[OSD([sQuery(id+"F0.wireOp",EDGE,"E7")])],"isStart":true});
            var Q8;
            Q8=makeQuery(id+"F1.opExtrude","SWEPT_EDGE",EDGE,{"disambiguationData":[OSD([sQuery(id+"F0.wireOp",EDGE,"E7"),sQuery(id+"F0.wireOp",EDGE,"E8")])]});
            var Q9;
            Q9=makeQuery(id+"F1.opExtrude","CAP_EDGE",EDGE,{"disambiguationData":[OSD([sQuery(id+"F0.wireOp",EDGE,"E8")])],"isStart":true});
            var Q10;
            Q10=makeQuery(id+"F1.opExtrude","CAP_EDGE",EDGE,{"disambiguationData":[OSD([sQuery(id+"F0.wireOp",EDGE,"E0")])],"isStart":false});
            var Q11;
            Q11=makeQuery(id+"F1.opExtrude","CAP_EDGE",EDGE,{"disambiguationData":[OSD([sQuery(id+"F0.wireOp",EDGE,"E1")])],"isStart":false});
            var Q12;
            Q12=makeQuery(id+"F1.opExtrude","CAP_EDGE",EDGE,{"disambiguationData":[OSD([sQuery(id+"F0.wireOp",EDGE,"E2")])],"isStart":false});
            var Q13;
            Q13=makeQuery(id+"F1.opExtrude","CAP_EDGE",EDGE,{"disambiguationData":[OSD([sQuery(id+"F0.wireOp",EDGE,"E3")])],"isStart":false});
            var Q14;
            Q14=makeQuery(id+"F1.opExtrude","CAP_EDGE",EDGE,{"disambiguationData":[OSD([sQuery(id+"F0.wireOp",EDGE,"E4")])],"isStart":false});
            var Q15;
            Q15=makeQuery(id+"F1.opExtrude","CAP_EDGE",EDGE,{"disambiguationData":[OSD([sQuery(id+"F0.wireOp",EDGE,"E5")])],"isStart":false});
            var Q16;
            Q16=makeQuery(id+"F1.opExtrude","CAP_EDGE",EDGE,{"disambiguationData":[OSD([sQuery(id+"F0.wireOp",EDGE,"E6")])],"isStart":false});
            var Q17;
            Q17=makeQuery(id+"F1.opExtrude","CAP_EDGE",EDGE,{"disambiguationData":[OSD([sQuery(id+"F0.wireOp",EDGE,"E7")])],"isStart":false});
            var Q18;
            Q18=makeQuery(id+"F1.opExtrude","CAP_EDGE",EDGE,{"disambiguationData":[OSD([sQuery(id+"F0.wireOp",EDGE,"E8")])],"isStart":false});
            var Q19;
            {var subQ0=sQuery(id+"F0.wireOp",EDGE,"E1");var subQ1=sQuery(id+"F0.wireOp",EDGE,"E0");Q19=makeQuery(id+"F10.opChamfer","BLEND_EDGE",EDGE,{"blendedFrom":[makeQuery(id+"F1.opExtrude","SWEPT_EDGE",EDGE,{"disambiguationData":[OSD([subQ1,subQ0])]}),makeQuery(id+"F1.opExtrude","CAP_FACE",FACE,{"disambiguationData":[OSD([subQ1,subQ0,sQuery(id+"F0.wireOp",EDGE,"E2"),sQuery(id+"F0.wireOp",EDGE,"E3"),sQuery(id+"F0.wireOp",EDGE,"E4"),sQuery(id+"F0.wireOp",EDGE,"E5"),sQuery(id+"F0.wireOp",EDGE,"E6"),sQuery(id+"F0.wireOp",EDGE,"E7"),sQuery(id+"F0.wireOp",EDGE,"E8"),sQuery(id+"F0.wireOp",EDGE,"E9")])],"isStart":true})],"blendedInto":[makeQuery(id+"F1.opExtrude","CAP_FACE",FACE,{"disambiguationData":[OSD([subQ1,subQ0,sQuery(id+"F0.wireOp",EDGE,"E2"),sQuery(id+"F0.wireOp",EDGE,"E3"),sQuery(id+"F0.wireOp",EDGE,"E4"),sQuery(id+"F0.wireOp",EDGE,"E5"),sQuery(id+"F0.wireOp",EDGE,"E6"),sQuery(id+"F0.wireOp",EDGE,"E7"),sQuery(id+"F0.wireOp",EDGE,"E8"),sQuery(id+"F0.wireOp",EDGE,"E9")])],"isStart":true})]});}
            var Q20;
            {var subQ0=sQuery(id+"F0.wireOp",EDGE,"E3");var subQ1=sQuery(id+"F0.wireOp",EDGE,"E2");Q20=makeQuery(id+"F10.opChamfer","BLEND_EDGE",EDGE,{"blendedFrom":[makeQuery(id+"F1.opExtrude","SWEPT_EDGE",EDGE,{"disambiguationData":[OSD([subQ1,subQ0])]}),makeQuery(id+"F1.opExtrude","CAP_FACE",FACE,{"disambiguationData":[OSD([sQuery(id+"F0.wireOp",EDGE,"E0"),sQuery(id+"F0.wireOp",EDGE,"E1"),subQ1,subQ0,sQuery(id+"F0.wireOp",EDGE,"E4"),sQuery(id+"F0.wireOp",EDGE,"E5"),sQuery(id+"F0.wireOp",EDGE,"E6"),sQuery(id+"F0.wireOp",EDGE,"E7"),sQuery(id+"F0.wireOp",EDGE,"E8"),sQuery(id+"F0.wireOp",EDGE,"E9")])],"isStart":true})],"blendedInto":[makeQuery(id+"F1.opExtrude","CAP_FACE",FACE,{"disambiguationData":[OSD([sQuery(id+"F0.wireOp",EDGE,"E0"),sQuery(id+"F0.wireOp",EDGE,"E1"),subQ1,subQ0,sQuery(id+"F0.wireOp",EDGE,"E4"),sQuery(id+"F0.wireOp",EDGE,"E5"),sQuery(id+"F0.wireOp",EDGE,"E6"),sQuery(id+"F0.wireOp",EDGE,"E7"),sQuery(id+"F0.wireOp",EDGE,"E8"),sQuery(id+"F0.wireOp",EDGE,"E9")])],"isStart":true})]});}
            var Q21;
            {var subQ0=sQuery(id+"F0.wireOp",EDGE,"E5");var subQ1=sQuery(id+"F0.wireOp",EDGE,"E4");Q21=makeQuery(id+"F10.opChamfer","BLEND_EDGE",EDGE,{"blendedFrom":[makeQuery(id+"F1.opExtrude","SWEPT_EDGE",EDGE,{"disambiguationData":[OSD([subQ1,subQ0])]}),makeQuery(id+"F1.opExtrude","CAP_FACE",FACE,{"disambiguationData":[OSD([sQuery(id+"F0.wireOp",EDGE,"E0"),sQuery(id+"F0.wireOp",EDGE,"E1"),sQuery(id+"F0.wireOp",EDGE,"E2"),sQuery(id+"F0.wireOp",EDGE,"E3"),subQ1,subQ0,sQuery(id+"F0.wireOp",EDGE,"E6"),sQuery(id+"F0.wireOp",EDGE,"E7"),sQuery(id+"F0.wireOp",EDGE,"E8"),sQuery(id+"F0.wireOp",EDGE,"E9")])],"isStart":true})],"blendedInto":[makeQuery(id+"F1.opExtrude","CAP_FACE",FACE,{"disambiguationData":[OSD([sQuery(id+"F0.wireOp",EDGE,"E0"),sQuery(id+"F0.wireOp",EDGE,"E1"),sQuery(id+"F0.wireOp",EDGE,"E2"),sQuery(id+"F0.wireOp",EDGE,"E3"),subQ1,subQ0,sQuery(id+"F0.wireOp",EDGE,"E6"),sQuery(id+"F0.wireOp",EDGE,"E7"),sQuery(id+"F0.wireOp",EDGE,"E8"),sQuery(id+"F0.wireOp",EDGE,"E9")])],"isStart":true})]});}
            var Q22;
            {var subQ0=sQuery(id+"F0.wireOp",EDGE,"E1");var subQ1=sQuery(id+"F0.wireOp",EDGE,"E0");Q22=makeQuery(id+"F10.opChamfer","BLEND_EDGE",EDGE,{"blendedFrom":[makeQuery(id+"F1.opExtrude","SWEPT_EDGE",EDGE,{"disambiguationData":[OSD([subQ1,subQ0])]}),makeQuery(id+"F1.opExtrude","CAP_FACE",FACE,{"disambiguationData":[OSD([subQ1,subQ0,sQuery(id+"F0.wireOp",EDGE,"E2"),sQuery(id+"F0.wireOp",EDGE,"E3"),sQuery(id+"F0.wireOp",EDGE,"E4"),sQuery(id+"F0.wireOp",EDGE,"E5"),sQuery(id+"F0.wireOp",EDGE,"E6"),sQuery(id+"F0.wireOp",EDGE,"E7"),sQuery(id+"F0.wireOp",EDGE,"E8"),sQuery(id+"F0.wireOp",EDGE,"E9")])],"isStart":false})],"blendedInto":[makeQuery(id+"F1.opExtrude","CAP_FACE",FACE,{"disambiguationData":[OSD([subQ1,subQ0,sQuery(id+"F0.wireOp",EDGE,"E2"),sQuery(id+"F0.wireOp",EDGE,"E3"),sQuery(id+"F0.wireOp",EDGE,"E4"),sQuery(id+"F0.wireOp",EDGE,"E5"),sQuery(id+"F0.wireOp",EDGE,"E6"),sQuery(id+"F0.wireOp",EDGE,"E7"),sQuery(id+"F0.wireOp",EDGE,"E8"),sQuery(id+"F0.wireOp",EDGE,"E9")])],"isStart":false})]});}
            var Q23;
            {var subQ0=sQuery(id+"F0.wireOp",EDGE,"E3");var subQ1=sQuery(id+"F0.wireOp",EDGE,"E2");Q23=makeQuery(id+"F10.opChamfer","BLEND_EDGE",EDGE,{"blendedFrom":[makeQuery(id+"F1.opExtrude","SWEPT_EDGE",EDGE,{"disambiguationData":[OSD([subQ1,subQ0])]}),makeQuery(id+"F1.opExtrude","CAP_FACE",FACE,{"disambiguationData":[OSD([sQuery(id+"F0.wireOp",EDGE,"E0"),sQuery(id+"F0.wireOp",EDGE,"E1"),subQ1,subQ0,sQuery(id+"F0.wireOp",EDGE,"E4"),sQuery(id+"F0.wireOp",EDGE,"E5"),sQuery(id+"F0.wireOp",EDGE,"E6"),sQuery(id+"F0.wireOp",EDGE,"E7"),sQuery(id+"F0.wireOp",EDGE,"E8"),sQuery(id+"F0.wireOp",EDGE,"E9")])],"isStart":false})],"blendedInto":[makeQuery(id+"F1.opExtrude","CAP_FACE",FACE,{"disambiguationData":[OSD([sQuery(id+"F0.wireOp",EDGE,"E0"),sQuery(id+"F0.wireOp",EDGE,"E1"),subQ1,subQ0,sQuery(id+"F0.wireOp",EDGE,"E4"),sQuery(id+"F0.wireOp",EDGE,"E5"),sQuery(id+"F0.wireOp",EDGE,"E6"),sQuery(id+"F0.wireOp",EDGE,"E7"),sQuery(id+"F0.wireOp",EDGE,"E8"),sQuery(id+"F0.wireOp",EDGE,"E9")])],"isStart":false})]});}
            var Q24;
            {var subQ0=sQuery(id+"F0.wireOp",EDGE,"E5");var subQ1=sQuery(id+"F0.wireOp",EDGE,"E4");Q24=makeQuery(id+"F10.opChamfer","BLEND_EDGE",EDGE,{"blendedFrom":[makeQuery(id+"F1.opExtrude","SWEPT_EDGE",EDGE,{"disambiguationData":[OSD([subQ1,subQ0])]}),makeQuery(id+"F1.opExtrude","CAP_FACE",FACE,{"disambiguationData":[OSD([sQuery(id+"F0.wireOp",EDGE,"E0"),sQuery(id+"F0.wireOp",EDGE,"E1"),sQuery(id+"F0.wireOp",EDGE,"E2"),sQuery(id+"F0.wireOp",EDGE,"E3"),subQ1,subQ0,sQuery(id+"F0.wireOp",EDGE,"E6"),sQuery(id+"F0.wireOp",EDGE,"E7"),sQuery(id+"F0.wireOp",EDGE,"E8"),sQuery(id+"F0.wireOp",EDGE,"E9")])],"isStart":false})],"blendedInto":[makeQuery(id+"F1.opExtrude","CAP_FACE",FACE,{"disambiguationData":[OSD([sQuery(id+"F0.wireOp",EDGE,"E0"),sQuery(id+"F0.wireOp",EDGE,"E1"),sQuery(id+"F0.wireOp",EDGE,"E2"),sQuery(id+"F0.wireOp",EDGE,"E3"),subQ1,subQ0,sQuery(id+"F0.wireOp",EDGE,"E6"),sQuery(id+"F0.wireOp",EDGE,"E7"),sQuery(id+"F0.wireOp",EDGE,"E8"),sQuery(id+"F0.wireOp",EDGE,"E9")])],"isStart":false})]});}
            var Q25;
            {var subQ0=sQuery(id+"F0.wireOp",EDGE,"E7");var subQ1=sQuery(id+"F0.wireOp",EDGE,"E6");Q25=makeQuery(id+"F11.opChamfer","BLEND_EDGE",EDGE,{"blendedFrom":[makeQuery(id+"F1.opExtrude","SWEPT_EDGE",EDGE,{"disambiguationData":[OSD([subQ1,subQ0])]}),makeQuery(id+"F1.opExtrude","CAP_FACE",FACE,{"disambiguationData":[OSD([sQuery(id+"F0.wireOp",EDGE,"E0"),sQuery(id+"F0.wireOp",EDGE,"E1"),sQuery(id+"F0.wireOp",EDGE,"E2"),sQuery(id+"F0.wireOp",EDGE,"E3"),sQuery(id+"F0.wireOp",EDGE,"E4"),sQuery(id+"F0.wireOp",EDGE,"E5"),subQ1,subQ0,sQuery(id+"F0.wireOp",EDGE,"E8"),sQuery(id+"F0.wireOp",EDGE,"E9")])],"isStart":false})],"blendedInto":[makeQuery(id+"F1.opExtrude","CAP_FACE",FACE,{"disambiguationData":[OSD([sQuery(id+"F0.wireOp",EDGE,"E0"),sQuery(id+"F0.wireOp",EDGE,"E1"),sQuery(id+"F0.wireOp",EDGE,"E2"),sQuery(id+"F0.wireOp",EDGE,"E3"),sQuery(id+"F0.wireOp",EDGE,"E4"),sQuery(id+"F0.wireOp",EDGE,"E5"),subQ1,subQ0,sQuery(id+"F0.wireOp",EDGE,"E8"),sQuery(id+"F0.wireOp",EDGE,"E9")])],"isStart":false})]});}
            var Q26;
            {var subQ0=sQuery(id+"F0.wireOp",EDGE,"E7");var subQ1=sQuery(id+"F0.wireOp",EDGE,"E6");Q26=makeQuery(id+"F11.opChamfer","BLEND_EDGE",EDGE,{"blendedFrom":[makeQuery(id+"F1.opExtrude","SWEPT_EDGE",EDGE,{"disambiguationData":[OSD([subQ1,subQ0])]}),makeQuery(id+"F1.opExtrude","CAP_FACE",FACE,{"disambiguationData":[OSD([sQuery(id+"F0.wireOp",EDGE,"E0"),sQuery(id+"F0.wireOp",EDGE,"E1"),sQuery(id+"F0.wireOp",EDGE,"E2"),sQuery(id+"F0.wireOp",EDGE,"E3"),sQuery(id+"F0.wireOp",EDGE,"E4"),sQuery(id+"F0.wireOp",EDGE,"E5"),subQ1,subQ0,sQuery(id+"F0.wireOp",EDGE,"E8"),sQuery(id+"F0.wireOp",EDGE,"E9")])],"isStart":true})],"blendedInto":[makeQuery(id+"F1.opExtrude","CAP_FACE",FACE,{"disambiguationData":[OSD([sQuery(id+"F0.wireOp",EDGE,"E0"),sQuery(id+"F0.wireOp",EDGE,"E1"),sQuery(id+"F0.wireOp",EDGE,"E2"),sQuery(id+"F0.wireOp",EDGE,"E3"),sQuery(id+"F0.wireOp",EDGE,"E4"),sQuery(id+"F0.wireOp",EDGE,"E5"),subQ1,subQ0,sQuery(id+"F0.wireOp",EDGE,"E8"),sQuery(id+"F0.wireOp",EDGE,"E9")])],"isStart":true})]});}
            fillet(context, id + "F13", {"entities" : qUnion([Q0, Q1, Q2, Q3, Q4, Q5, Q6, Q7, Q8, Q9, Q10, Q11, Q12, Q13, Q14, Q15, Q16, Q17, Q18, Q19, Q20, Q21, Q22, Q23, Q24, Q25, Q26]), "radius" : 2.54 * mm, "tangentPropagation" : true, "allowEdgeOverflow" : false});
        }
    });
